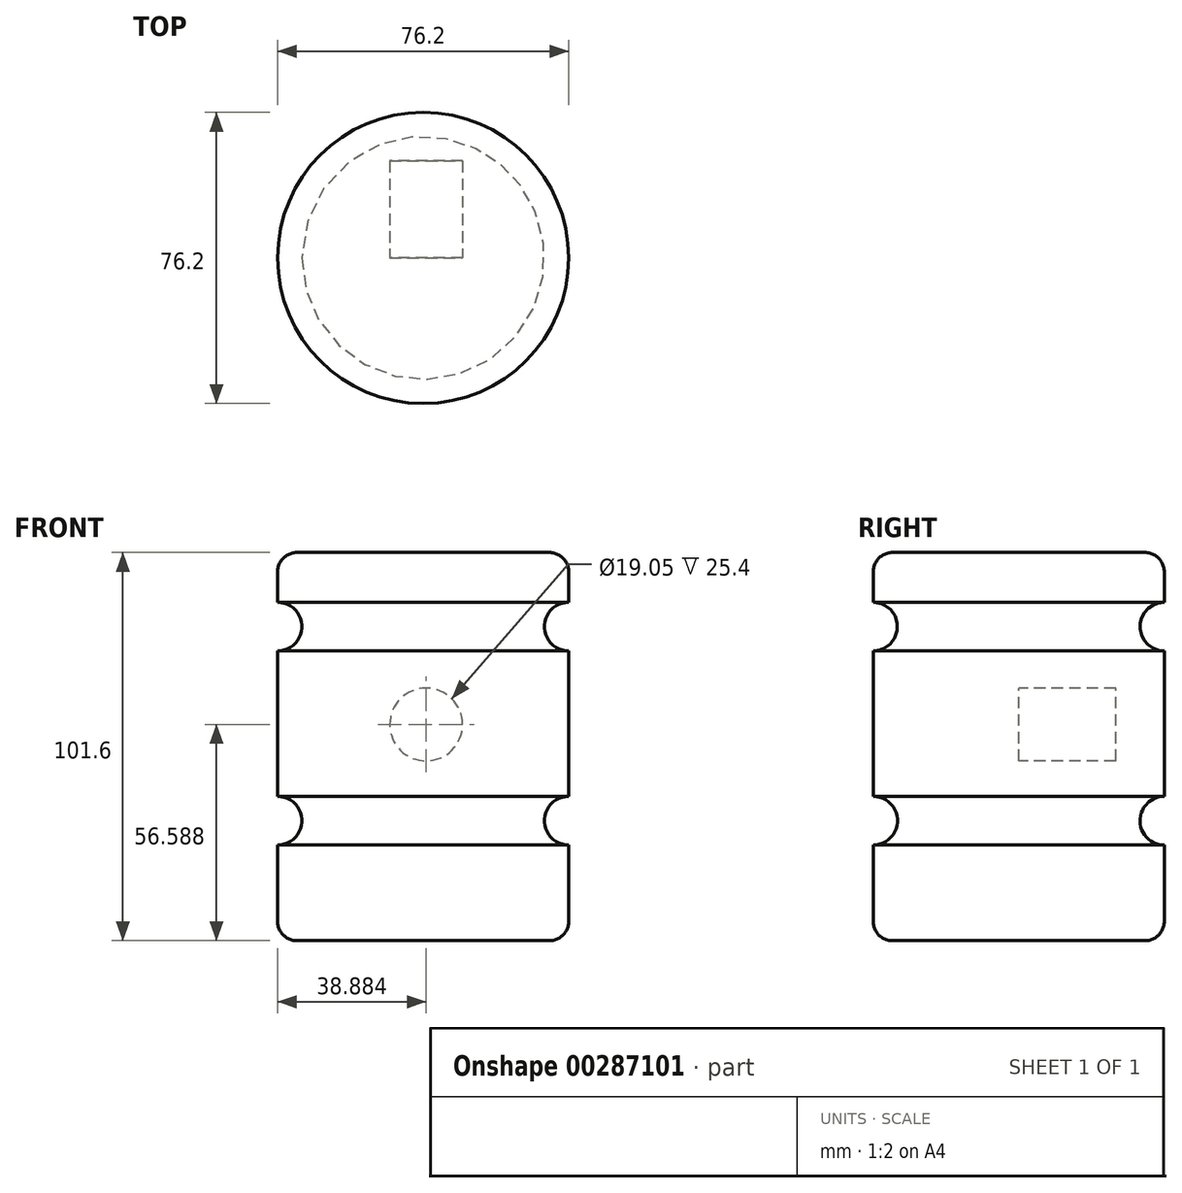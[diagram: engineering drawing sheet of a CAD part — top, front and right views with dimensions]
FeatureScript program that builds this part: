
annotation { "Feature Type Name" : "Feature", "Feature Type Description" : "" }
export const myFeature = defineFeature(function(context is Context, id is Id, definition is map)
    precondition{}
    {
        {
            var Q0;
            Q0=qCreatedBy(makeId("Front.planeOp"),FACE);
            var sketch = newSketch(context, id + "F0", { "sketchPlane" : qUnion([Q0])});
            skLineSegment(sketch, "E0.bottom", {"start": v(0, 0) * mm, "end": v(-38.1, 0) * mm});
            skLineSegment(sketch, "E0.top", {"start": v(0, 101.6) * mm, "end": v(-38.1, 101.6) * mm});
            skLineSegment(sketch, "E0.left", {"start": v(0, 0) * mm, "end": v(0, 25.06) * mm});
            skLineSegment(sketch, "E0.right", {"start": v(-38.1, 0) * mm, "end": v(-38.1, 101.6) * mm});
            skArc(sketch, "E1", {"start": v(0, 88.56) * mm, "mid": v(-6.35, 82.2) * mm, "end": v(0, 75.86) * mm});
            skArc(sketch, "E2", {"start": v(0, 37.76) * mm, "mid": v(-6.35, 31.41) * mm, "end": v(0, 25.06) * mm});
            skLineSegment(sketch, "E3.trimOffspring", {"start": v(0, 37.76) * mm, "end": v(0, 75.86) * mm});
            skLineSegment(sketch, "E4.trimOffspring", {"start": v(0, 88.56) * mm, "end": v(0, 101.6) * mm});
            skSolve(sketch);
        }
        {
            var Q0;
            Q0=makeQuery(id+"F0.imprint","IMPRINT",FACE,{"disambiguationData":[TD([[makeQuery(id+"F0.imprint","IMPRINT",EDGE,{"derivedFrom":sQuery(id+"F0.wireOp",EDGE,"E0.bottom")}),-1.0]])]});
            var Q1;
            Q1=sQuery(id+"F0.wireOp",EDGE,"E0.right");
            revolve(context, id + "F1", {"entities" : qUnion([Q0]), "axis" : qUnion([Q1]), "revolveType" : RevolveType.FULL});
        }
        {
            var Q0;
            Q0=qCreatedBy(makeId("Front.planeOp"),FACE);
            var sketch = newSketch(context, id + "F2", { "sketchPlane" : qUnion([Q0])});
            skCircle(sketch, "E5", {"center": v(-37.32, 56.59) * mm, "radius": 9.53 * mm});
            skSolve(sketch);
        }
        {
            var Q0;
            Q0 = qSketchRegion(id + "F2", true);
            extrude(context, id + "F3", {"entities" : qUnion([Q0]), "operationType" : NewBodyOperationType.REMOVE, "oppositeDirection" : true, "depth" : 25.4 * mm});
        }
        {
            var Q0;
            Q0 = qSketchRegion(id + "F2", true);
            extrude(context, id + "F4", {"entities" : qUnion([Q0]), "operationType" : NewBodyOperationType.REMOVE, "oppositeDirection" : true, "depth" : 25.4 * mm});
        }
        {
            var Q0;
            Q0=makeQuery(id+"F1.opRevolve","SWEPT_EDGE",EDGE,{"disambiguationData":[OSD([sQuery(id+"F0.wireOp",EDGE,"E0.top"),sQuery(id+"F0.wireOp",EDGE,"E4.trimOffspring")])]});
            fillet(context, id + "F5", {"entities" : qUnion([Q0]), "radius" : 5.08 * mm, "tangentPropagation" : true, "allowEdgeOverflow" : false});
        }
        {
            var Q0;
            Q0=makeQuery(id+"F1.opRevolve","SWEPT_EDGE",EDGE,{"disambiguationData":[OSD([sQuery(id+"F0.wireOp",EDGE,"E0.bottom"),sQuery(id+"F0.wireOp",EDGE,"E0.left")])]});
            fillet(context, id + "F6", {"entities" : qUnion([Q0]), "radius" : 5.08 * mm, "tangentPropagation" : true, "allowEdgeOverflow" : false});
        }
    });
